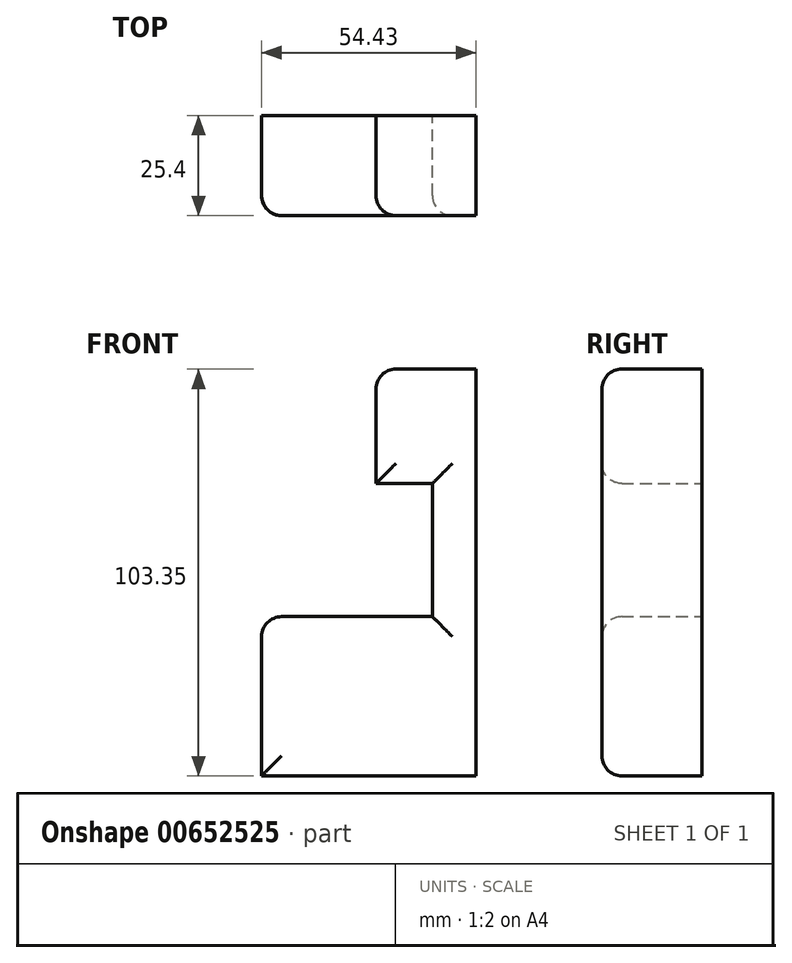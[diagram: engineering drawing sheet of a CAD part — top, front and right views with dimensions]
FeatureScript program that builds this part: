
annotation { "Feature Type Name" : "Feature", "Feature Type Description" : "" }
export const myFeature = defineFeature(function(context is Context, id is Id, definition is map)
    precondition{}
    {
        {
            var Q0;
            Q0=qCreatedBy(makeId("Front.planeOp"),FACE);
            var sketch = newSketch(context, id + "F0", { "sketchPlane" : qUnion([Q0])});
            skLineSegment(sketch, "E0", {"start": v(0, 52.78) * mm, "end": v(-25.38, 52.78) * mm});
            skLineSegment(sketch, "E1", {"start": v(-25.38, 52.78) * mm, "end": v(-25.38, 23.72) * mm});
            skLineSegment(sketch, "E2", {"start": v(-25.38, 23.72) * mm, "end": v(-11.03, 23.72) * mm});
            skLineSegment(sketch, "E3", {"start": v(-11.03, 23.72) * mm, "end": v(-11.03, -10.11) * mm});
            skLineSegment(sketch, "E4", {"start": v(-11.03, -10.11) * mm, "end": v(-54.43, -10.11) * mm});
            skLineSegment(sketch, "E5", {"start": v(-54.43, -10.11) * mm, "end": v(-54.43, -50.57) * mm});
            skLineSegment(sketch, "E6", {"start": v(-54.43, -50.57) * mm, "end": v(0, -50.57) * mm});
            skLineSegment(sketch, "E7", {"start": v(0, -50.57) * mm, "end": v(0, 52.78) * mm});
            skSolve(sketch);
        }
        {
            var Q0;
            Q0=makeQuery(id+"F0.imprint","IMPRINT",FACE,{"disambiguationData":[TD([[makeQuery(id+"F0.imprint","IMPRINT",EDGE,{"derivedFrom":sQuery(id+"F0.wireOp",EDGE,"E0")}),1.0]])]});
            extrude(context, id + "F1", {"entities" : qUnion([Q0]), "depth" : 25.4 * mm, "offsetDistance" : 25.4 * mm});
        }
        {
            var Q0;
            Q0=makeQuery(id+"F1.opExtrude","CAP_EDGE",EDGE,{"disambiguationData":[OSD([sQuery(id+"F0.wireOp",EDGE,"E0")])],"isStart":false});
            fillet(context, id + "F2", {"entities" : qUnion([Q0]), "radius" : 5.08 * mm, "tangentPropagation" : true, "allowEdgeOverflow" : false});
        }
        {
            var Q0;
            Q0=makeQuery(id+"F1.opExtrude","CAP_EDGE",EDGE,{"disambiguationData":[OSD([sQuery(id+"F0.wireOp",EDGE,"E6")])],"isStart":false});
            var Q1;
            Q1=makeQuery(id+"F1.opExtrude","CAP_EDGE",EDGE,{"disambiguationData":[OSD([sQuery(id+"F0.wireOp",EDGE,"E5")])],"isStart":false});
            var Q2;
            Q2=makeQuery(id+"F1.opExtrude","CAP_EDGE",EDGE,{"disambiguationData":[OSD([sQuery(id+"F0.wireOp",EDGE,"E4")])],"isStart":false});
            var Q3;
            Q3=makeQuery(id+"F1.opExtrude","CAP_EDGE",EDGE,{"disambiguationData":[OSD([sQuery(id+"F0.wireOp",EDGE,"E3")])],"isStart":false});
            var Q4;
            Q4=makeQuery(id+"F1.opExtrude","CAP_EDGE",EDGE,{"disambiguationData":[OSD([sQuery(id+"F0.wireOp",EDGE,"E1")])],"isStart":false});
            var Q5;
            Q5=makeQuery(id+"F1.opExtrude","CAP_EDGE",EDGE,{"disambiguationData":[OSD([sQuery(id+"F0.wireOp",EDGE,"E2")])],"isStart":false});
            fillet(context, id + "F3", {"entities" : qUnion([Q0, Q1, Q2, Q3, Q4, Q5]), "radius" : 5.08 * mm, "tangentPropagation" : true, "allowEdgeOverflow" : false});
        }
        {
            var Q0;
            Q0=makeQuery(id+"F1.opExtrude","SWEPT_EDGE",EDGE,{"disambiguationData":[OSD([sQuery(id+"F0.wireOp",EDGE,"E4"),sQuery(id+"F0.wireOp",EDGE,"E5")])]});
            fillet(context, id + "F4", {"entities" : qUnion([Q0]), "radius" : 5.08 * mm, "tangentPropagation" : true, "allowEdgeOverflow" : false});
        }
    });
